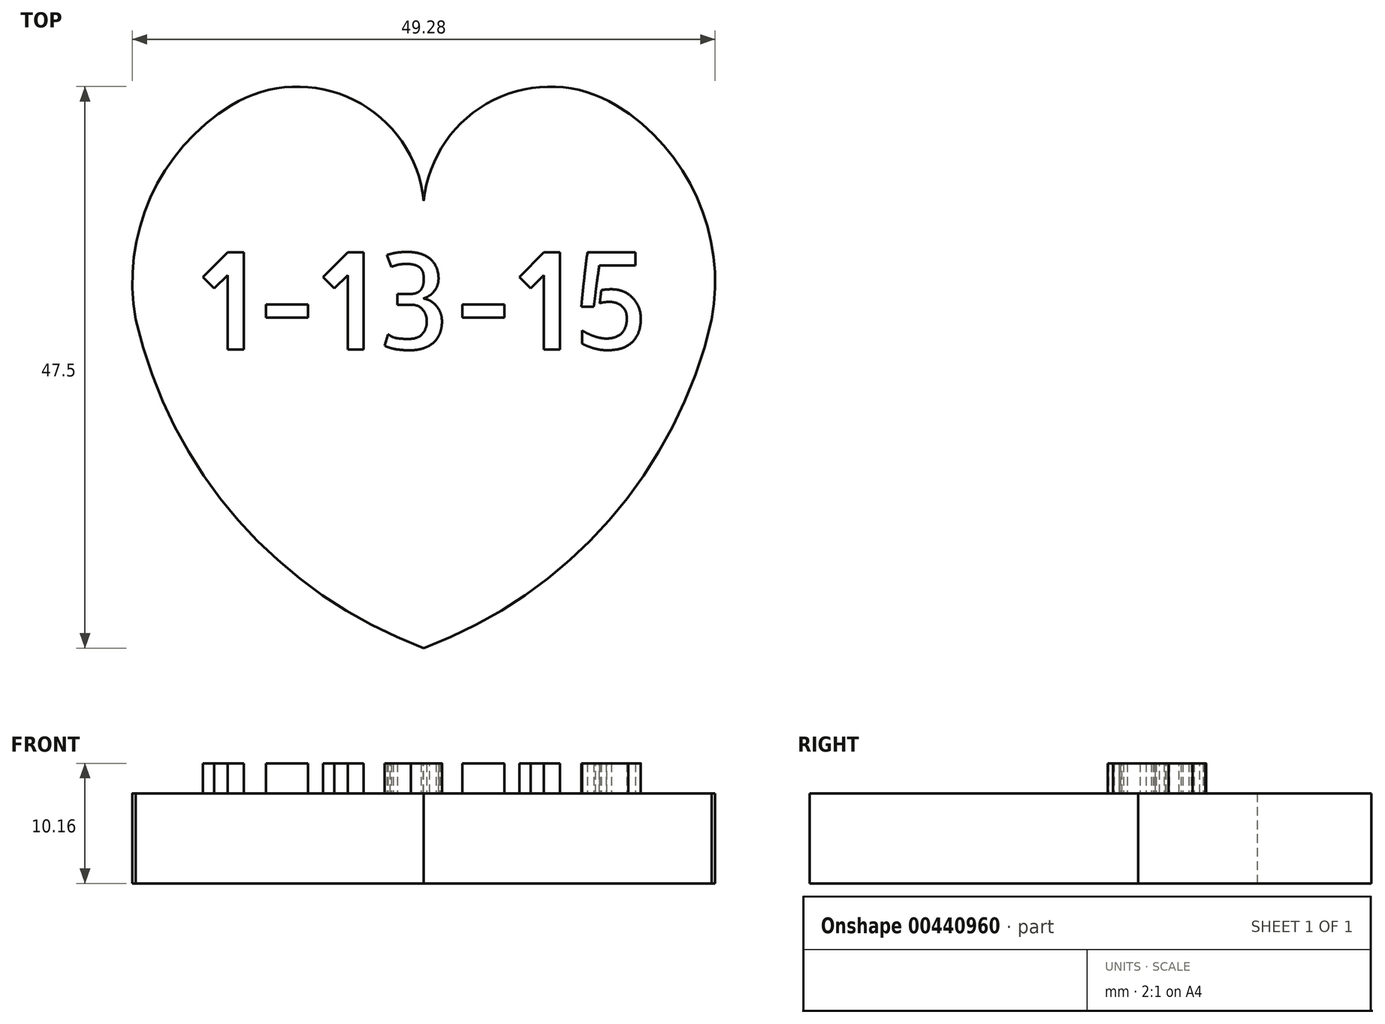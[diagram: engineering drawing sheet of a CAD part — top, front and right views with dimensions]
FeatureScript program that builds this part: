
annotation { "Feature Type Name" : "Feature", "Feature Type Description" : "" }
export const myFeature = defineFeature(function(context is Context, id is Id, definition is map)
    precondition{}
    {
        {
            var Q0;
            Q0=qCreatedBy(makeId("Top.planeOp"),FACE);
            var sketch = newSketch(context, id + "F0", { "sketchPlane" : qUnion([Q0])});
            skArc(sketch, "E0", {"start": v(-24.36, 27.79) * mm, "mid": v(-15.68, 10.82) * mm, "end": v(0, 0) * mm});
            skArc(sketch, "E1", {"start": v(-16.26, 45.94) * mm, "mid": v(-23.11, 38.11) * mm, "end": v(-24.36, 27.79) * mm});
            skArc(sketch, "E2", {"start": v(0, 37.84) * mm, "mid": v(-5.9, 46.37) * mm, "end": v(-16.26, 45.94) * mm});
            skArc(sketch, "E3.MirrorCS", {"start": v(0, 37.84) * mm, "mid": v(5.9, 46.37) * mm, "end": v(16.26, 45.94) * mm});
            skArc(sketch, "E4.MirrorCS", {"start": v(16.26, 45.94) * mm, "mid": v(23.11, 38.11) * mm, "end": v(24.36, 27.79) * mm});
            skArc(sketch, "E5.MirrorCS", {"start": v(24.36, 27.79) * mm, "mid": v(15.68, 10.82) * mm, "end": v(0, 0) * mm});
            skSolve(sketch);
        }
        {
            var Q0;
            Q0=makeQuery(id+"F0.imprint","IMPRINT",FACE,{"disambiguationData":[TD([[makeQuery(id+"F0.imprint","IMPRINT",EDGE,{"derivedFrom":sQuery(id+"F0.wireOp",EDGE,"E0")}),1.0]])]});
            extrude(context, id + "F1", {"entities" : qUnion([Q0]), "depth" : 7.62 * mm});
        }
        {
            var Q0;
            Q0=makeQuery(id+"F1.opExtrude","CAP_FACE",FACE,{"disambiguationData":[OSD([sQuery(id+"F0.wireOp",EDGE,"E0"),sQuery(id+"F0.wireOp",EDGE,"E1"),sQuery(id+"F0.wireOp",EDGE,"E2"),sQuery(id+"F0.wireOp",EDGE,"E3.MirrorCS"),sQuery(id+"F0.wireOp",EDGE,"E4.MirrorCS"),sQuery(id+"F0.wireOp",EDGE,"E5.MirrorCS")])],"isStart":false});
            var sketch = newSketch(context, id + "F2", { "sketchPlane" : qUnion([Q0])});
            skText(sketch, "E6", { "text": "1-13-15", "fontName": "AllertaStencil-Regular.ttf"});
            const initialGuessF2  = {"E6": [-0.019, 0.02525, 1, 0, 0.00822]};
            skSetInitialGuess(sketch, initialGuessF2);
            skSolve(sketch);
        }
        {
            var Q0;
            Q0 = qSketchRegion(id + "F2", true);
            extrude(context, id + "F3", {"entities" : qUnion([Q0]), "operationType" : NewBodyOperationType.ADD, "depth" : 2.54 * mm});
        }
    });
